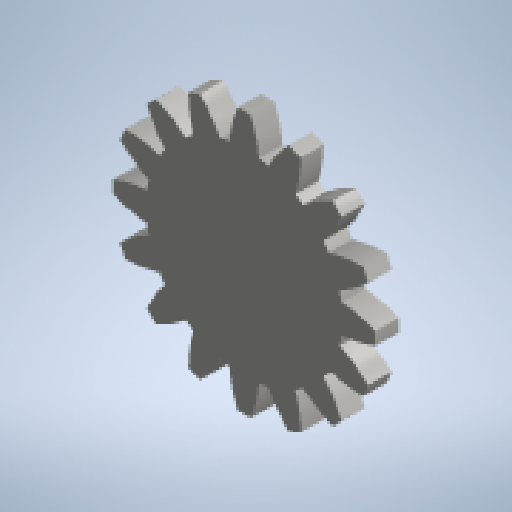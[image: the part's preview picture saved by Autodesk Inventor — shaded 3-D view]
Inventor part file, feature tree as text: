
AUTODESK INVENTOR PART (.ipt)
format: ipt  version: 2025 (Build 290162010, 162A)  size: 233,984 bytes
history: native  units: mm (DEFAULTED — no unit token found)
features: plane x3, other x3, extrude x1, sketch x1
ambient origin geometry x8: Origin, YZ Plane, XZ Plane, XY Plane, X Axis, Y Axis, Z Axis, Center Point
bodies: Solid1 (feature_tree)
feature tree (8):
  extrude  "Extrusion1"  Depth=20.0mm TaperAngle=0.0deg
  plane  "Work Plane2"
  plane  "Work Plane8"
  plane  "Work Plane9"
  other  "Spur Gear"
  sketch  "Sketch1"  dims[d0=225.0mm d1=20.0mm d2=0.0mm d3=200.0mm d4=10.0mm d5=0.0mm d16=800.0mm d17=0.0mm d34=1.963495mm d39=0.0mm d41=0.0mm d43=800.0mm d46=800.0mm d47=0.0mm d48=0.0mm]
  other  "Srf1"
  other  "Pitch Diameter"
